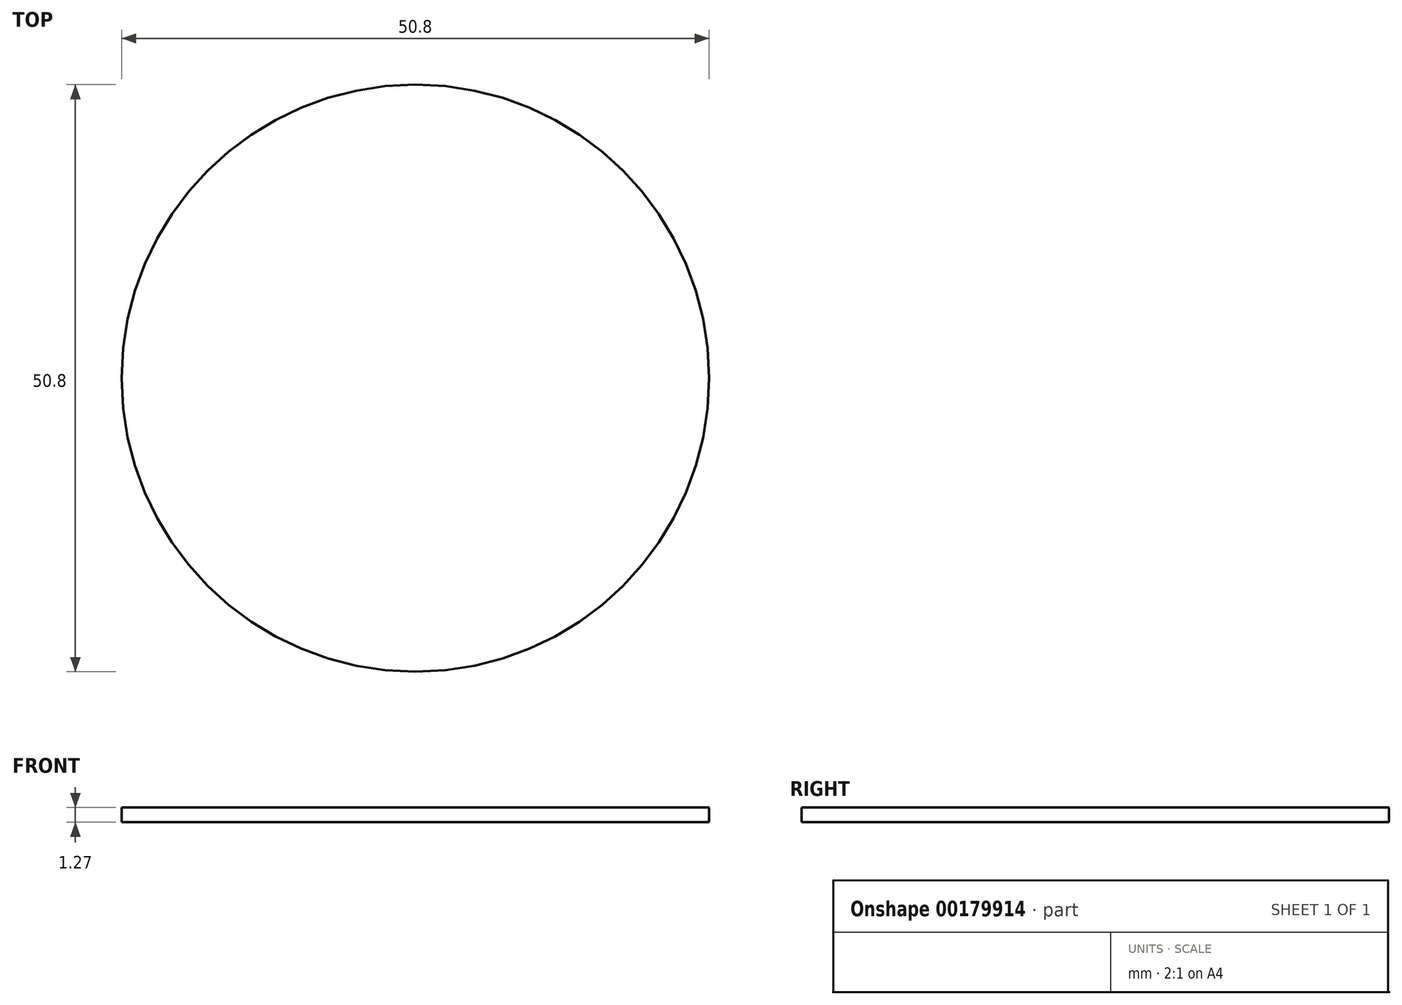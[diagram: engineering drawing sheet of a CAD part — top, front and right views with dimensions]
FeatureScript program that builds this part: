
annotation { "Feature Type Name" : "Feature", "Feature Type Description" : "" }
export const myFeature = defineFeature(function(context is Context, id is Id, definition is map)
    precondition{}
    {
        {
            var Q0;
            Q0=qCreatedBy(makeId("Top.planeOp"),FACE);
            var sketch = newSketch(context, id + "F0", { "sketchPlane" : qUnion([Q0])});
            skCircle(sketch, "E0", {"center": v(0, 0) * mm, "radius": 25.4 * mm});
            skSolve(sketch);
        }
        {
            var Q0;
            Q0=makeQuery(id+"F0.imprint","IMPRINT",FACE,{"disambiguationData":[TD([[makeQuery(id+"F0.imprint","IMPRINT",EDGE,{"derivedFrom":sQuery(id+"F0.wireOp",EDGE,"E0")}),1.0]])]});
            cPlane(context, id + "F1", {"entities" : qUnion([Q0]), "cplaneType" : CPlaneType.OFFSET, "offset" : 25.4 * mm, "width" : 152.4 * mm, "height" : 152.4 * mm});
        }
        {
            var Q0;
            Q0=qCreatedBy(id+"F1.planeOp",FACE);
            var sketch = newSketch(context, id + "F2", { "sketchPlane" : qUnion([Q0])});
            skCircle(sketch, "E1", {"center": v(0, 0) * mm, "radius": 38.1 * mm});
            skSolve(sketch);
        }
        {
            var Q0;
            Q0=makeQuery(id+"F2.imprint","IMPRINT",FACE,{"disambiguationData":[TD([[makeQuery(id+"F2.imprint","IMPRINT",EDGE,{"derivedFrom":sQuery(id+"F2.wireOp",EDGE,"E1")}),1.0]])]});
            var Q1;
            Q1=makeQuery(id+"F0.imprint","IMPRINT",FACE,{"disambiguationData":[TD([[makeQuery(id+"F0.imprint","IMPRINT",EDGE,{"derivedFrom":sQuery(id+"F0.wireOp",EDGE,"E0")}),1.0]])]});
            var Q2;
            Q2=makeQuery(id+"F0.imprint","IMPRINT",FACE,{"disambiguationData":[TD([[makeQuery(id+"F0.imprint","IMPRINT",EDGE,{"derivedFrom":sQuery(id+"F0.wireOp",EDGE,"E0")}),1.0]])]});
            var Q3;
            Q3=makeQuery(id+"F2.imprint","IMPRINT",FACE,{"disambiguationData":[TD([[makeQuery(id+"F2.imprint","IMPRINT",EDGE,{"derivedFrom":sQuery(id+"F2.wireOp",EDGE,"E1")}),1.0]])]});
            loft(context, id + "F3", {"bodyType" : ToolBodyType.SURFACE, "sheetProfilesArray" : [{ "sheetProfileEntities" : qUnion([Q0]) }, { "sheetProfileEntities" : qUnion([Q1]) }], "wireProfilesArray" : [{ "wireProfileEntities" : qUnion([Q2]) }, { "wireProfileEntities" : qUnion([Q3]) }]});
        }
        {
            var Q0;
            Q0=makeQuery(id+"F0.imprint","IMPRINT",FACE,{"disambiguationData":[TD([[makeQuery(id+"F0.imprint","IMPRINT",EDGE,{"derivedFrom":sQuery(id+"F0.wireOp",EDGE,"E0")}),1.0]])]});
            extrude(context, id + "F4", {"entities" : qUnion([Q0]), "oppositeDirection" : true, "depth" : 1.27 * mm});
        }
    });
